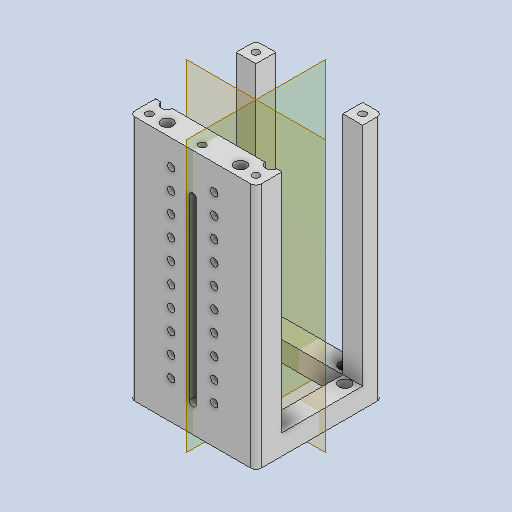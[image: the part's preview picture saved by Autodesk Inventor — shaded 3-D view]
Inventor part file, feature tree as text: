
AUTODESK INVENTOR PART (.ipt)
format: ipt  version: 2023 (Build 270158000, 158)  size: 273,920 bytes
history: native  units: mm
features: sketch x7, extrude x6, plane x2, other x2, fillet x1, hole x1, reference x1
ambient origin geometry x8: Origin, YZ Plane, XZ Plane, XY Plane, X Axis, Y Axis, Z Axis, Center Point
bodies: Solid1 (feature_tree)
feature tree (20):
  extrude  "Extrusion1"  Depth=49.8mm
  extrude  "Extrusion2"  Depth=8.0mm TaperAngle=0.0deg
  extrude  "Extrusion3"  Depth=97.0mm TaperAngle=0.0deg
  extrude  "Extrusion4"  Depth=2.9mm
  extrude  "Extrusion5"  Depth=23.45mm
  fillet  "Fillet1"  [1 undecoded]
  extrude  "Extrusion6"  Depth=2.9mm
  plane  "Arbeitsebene1"
  plane  "Arbeitsebene2"
  hole  "Bohrung1"  [1 undecoded]
  sketch  "Sketch1"  dims[d0=49.8mm d1=49.8mm]
  sketch  "Sketch3"  dims[d2=7.8mm d3=8.0mm d4=0.0mm]
  sketch  "Sketch4"  dims[d6=10.23mm d7=97.0mm d8=0.0mm]
  sketch  "Sketch5"  dims[d9=2.9mm d10=70.0mm]
  sketch  "Sketch6"  dims[d11=23.45mm d12=11.0mm d13=0.0mm d14=0.0mm]
  sketch  "Sketch7"  dims[d15=2.9mm d16=7.05mm]
  sketch  "Skizze8"  dims[d17=2.9mm d18=7.05mm d19=10.0mm d20=10.0mm d21=70.0mm d23=8.0mm d24=10.0mm d26=10.0mm d28=2.8mm d29=2.8mm d30=20.0mm d31=0.0mm d35=10.0mm d36=0.0mm d37=2.8mm d38=3.7mm d39=24.9mm d40=2.0mm d41=10.0mm d42=0.0mm d43=4.6mm d44=6.0mm d45=4.0mm d46=2.0mm d47=90.0deg d48=8.0mm d49=20.594885mm d50=40.0mm d52=8.0mm d53=10.0mm d55=10.0mm d57=0.5mm d58=0.872665mm d59=0.5mm d60=0.872665mm]
  reference  "Referenz1"
  other  "Assembly_Cube_Z-Stage_NEMA11_china_Borstel.iam"
  other  "10_Base_puzzle_IM:1"
note: 2 required parameter values undecoded (feature->parameter linkage not recoverable at this tier; creation-order binding heuristic only, values carry confidence <= 0.55)
